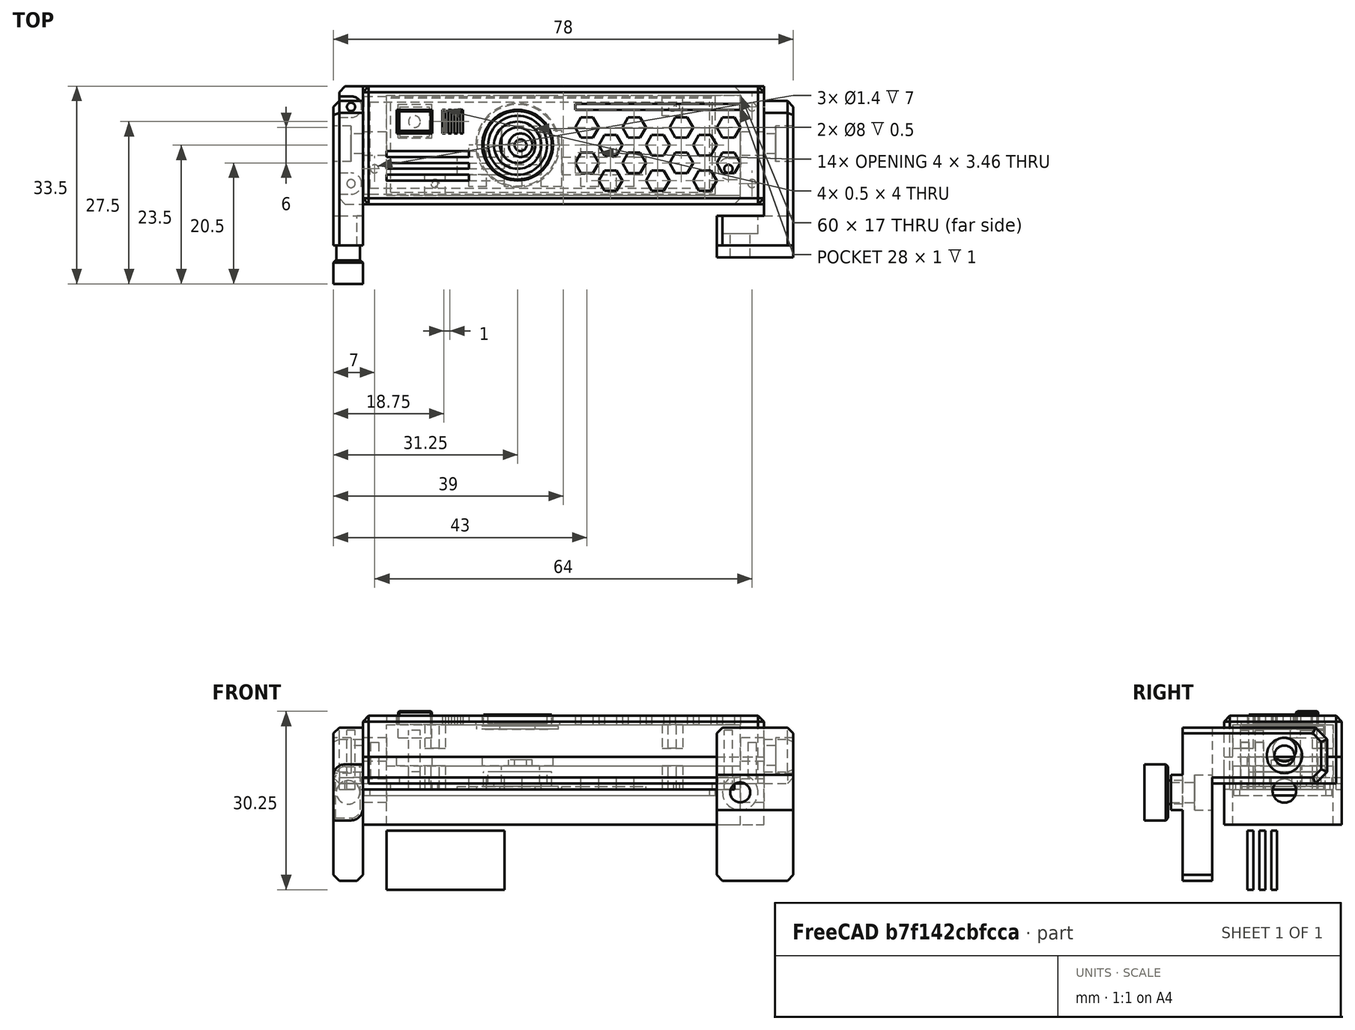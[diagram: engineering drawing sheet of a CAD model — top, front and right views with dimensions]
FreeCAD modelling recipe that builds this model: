
FCSTD DOCUMENT  (FreeCAD 0.18R16146 (Git))
Label: camera-body
License: All rights reserved
LicenseURL: http://en.wikipedia.org/wiki/All_rights_reserved
objects: Part::Box×40, Part::Cylinder×34, Part::Cut×31, Part::MultiFuse×22, Part::Feature×21, Part::Chamfer×11, Part::Fillet×1
note: 160 computed .brp shape members not serialized (recipe doc carries the construction recipe); baked Part::Feature solids carry a one-line shape summary decoded from their .brp

FEATURE [Part::Box] Box  label="Cube"
  AttacherType = Attacher::AttachEngine3D
  Height = 1
  Length = 54.5
  Width = 16
FEATURE [Part::Cylinder] Cylinder
  Angle = 360
  AttacherType = Attacher::AttachEngine3D
  Height = 10
  Placement = pos=(7.5,1.5,0) rot=(0,0,1;0rad)
  Radius = 0.7
FEATURE [Part::Cylinder] Cylinder001
  Angle = 360
  AttacherType = Attacher::AttachEngine3D
  Height = 10
  Placement = pos=(47.75,14.5,0) rot=(0,0,1;0rad)
  Radius = 0.7
FEATURE [Part::Cylinder] Cylinder002
  Angle = 360
  AttacherType = Attacher::AttachEngine3D
  Height = 10
  Placement = pos=(48.5,14.5,0) rot=(0,0,1;0rad)
  Radius = 0.5
FEATURE [Part::Cylinder] Cylinder003
  Angle = 360
  AttacherType = Attacher::AttachEngine3D
  Height = 10
  Placement = pos=(7.5,1.5,0) rot=(0,0,1;0rad)
  Radius = 0.5
FEATURE [Part::MultiFuse] Fusion
  Shapes = -> [Cylinder003,Cylinder002]
FEATURE [Part::Cut] Cut
  Base = -> Box
  Tool = -> Fusion
FEATURE [Part::Cylinder] Cylinder004
  Angle = 360
  AttacherType = Attacher::AttachEngine3D
  Height = 3
  Placement = pos=(4,12,0) rot=(0,0,1;0rad)
  Radius = 1
FEATURE [Part::Box] Box001  label="Cube001"
  AttacherType = Attacher::AttachEngine3D
  Height = 2
  Length = 5
  Placement = pos=(1.5,9.5,0) rot=(0,0,1;0rad)
  Width = 5
FEATURE [Part::Box] Box002  label="Cube002"
  AttacherType = Attacher::AttachEngine3D
  Height = 4
  Length = 6.5
  Placement = pos=(18.75,4.75,0) rot=(0,0,1;0rad)
  Width = 6.5
FEATURE [Part::Cylinder] Cylinder005
  Angle = 360
  AttacherType = Attacher::AttachEngine3D
  Height = 5
  Placement = pos=(22,8,0) rot=(0,0,1;0rad)
  Radius = 2
FEATURE [Part::Cylinder] Cylinder006
  Angle = 360
  AttacherType = Attacher::AttachEngine3D
  Height = 5
  Placement = pos=(22,8,0) rot=(0,0,1;0rad)
  Radius = 1
FEATURE [Part::Cut] Cut001
  Base = -> Cylinder005
  Tool = -> Cylinder006
FEATURE [Part::MultiFuse] Fusion001
  Shapes = -> [Cut001,Box002]
FEATURE [Part::MultiFuse] Fusion002  label="pcb-pred"
  Placement = pos=(-27.25,0,0) rot=(0,0,1;0rad)
  Shapes = -> [Fusion001,Box001,Cylinder004,Cut]
FEATURE [Part::Box] Box003  label="Cube003"
  AttacherType = Attacher::AttachEngine3D
  Height = 11.5
  Length = 68
  Placement = pos=(-32,-2,-6) rot=(0,0,1;0rad)
  Width = 20
FEATURE [Part::Box] Box004  label="Cube004"
  AttacherType = Attacher::AttachEngine3D
  Height = 10
  Length = 60
  Placement = pos=(-28,-0.5,-6) rot=(0,0,1;0rad)
  Width = 17
FEATURE [Part::Cylinder] Cylinder007
  Angle = 360
  AttacherType = Attacher::AttachEngine3D
  Height = 10
  Placement = pos=(-5.75,8,0) rot=(0,0,1;0rad)
  Radius = 3.2
FEATURE [Part::Cylinder] Cylinder008
  Angle = 360
  AttacherType = Attacher::AttachEngine3D
  Height = 10
  Placement = pos=(-23.25,12,0) rot=(0,0,1;0rad)
  Radius = 1
FEATURE [Part::Box] Box005  label="Cube005"
  AttacherType = Attacher::AttachEngine3D
  Height = 5
  Length = 3.5
  Placement = pos=(-21.5,-2,0) rot=(0,0,1;0rad)
  Width = 5
FEATURE [Part::Box] Box006  label="Cube006"
  AttacherType = Attacher::AttachEngine3D
  Height = 5
  Length = 3.5
  Placement = pos=(18.75,13,0) rot=(0,0,1;0rad)
  Width = 5
FEATURE [Part::MultiFuse] Fusion003003
  Placement = pos=(-27.25,0,-6) rot=(0,0,1;0rad)
  Shapes = -> [Cylinder,Cylinder001]
FEATURE [Part::Cut] Cut002
  Base = -> Box003
  Tool = -> Box004
FEATURE [Part::Cut] Cut003
  Base = -> Cut002
  Tool = -> Cylinder007
FEATURE [Part::MultiFuse] Fusion003004
  Shapes = -> [Box005,Box006]
FEATURE [Part::MultiFuse] Fusion003005
  Shapes = -> [Cut003,Fusion003004]
FEATURE [Part::Cut] Cut004
  Base = -> Fusion003005
  Tool = -> Fusion003003
FEATURE [Part::Box] Box007  label="Cube007"
  AttacherType = Attacher::AttachEngine3D
  Height = 10
  Length = 6
  Placement = pos=(-26.25,10,0) rot=(0,0,1;0rad)
  Width = 4
FEATURE [Part::Cut] Cut005
  Base = -> Cut004
  Tool = -> Box007
FEATURE [Part::Cylinder] Cylinder009
  Angle = 360
  AttacherType = Attacher::AttachEngine3D
  Height = 10
  Placement = pos=(-5.75,8,0) rot=(0,0,1;0rad)
  Radius = 6
FEATURE [Part::Cut] Cut006
  Base = -> Cut005
  Tool = -> Cylinder009
FEATURE [Part::Cylinder] Cylinder010
  Angle = 360
  AttacherType = Attacher::AttachEngine3D
  Height = 10
  Placement = pos=(-27,8.25,-0.25) rot=(0,-1,0;1.5708rad)
  Radius = 2
FEATURE [Part::Cylinder] Cylinder011
  Angle = 360
  AttacherType = Attacher::AttachEngine3D
  Height = 10
  Placement = pos=(37,8.25,-0.25) rot=(0,-1,0;1.5708rad)
  Radius = 2
FEATURE [Part::MultiFuse] Fusion003006
  Shapes = -> [Cylinder011,Cylinder010]
FEATURE [Part::Cut] Cut007
  Base = -> Cut006
  Tool = -> Fusion003006
FEATURE [Part::Feature] Cut007001  label="Cut008"
  shape: bbox 68 x 20 x 11.5 mm, 30 faces (baked)
FEATURE [Part::Chamfer] Chamfer
  Base = -> Cut007001
  Edges = 8 edges r=1: [Edge1,Edge2,Edge4,Edge6,Edge7,Edge8,Edge23,Edge24]
  Placement = pos=(1e-15,0,-7) rot=(0,1,0;3.14159rad)
FEATURE [Part::Cylinder] Cylinder012
  Angle = 360
  AttacherType = Attacher::AttachEngine3D
  Height = 10
  Placement = pos=(-34,14.5,0) rot=(0,0,1;0rad)
  Radius = 0.7
FEATURE [Part::Cylinder] Cylinder013
  Angle = 360
  AttacherType = Attacher::AttachEngine3D
  Height = 10
  Placement = pos=(-34,1.5,0) rot=(0,0,1;0rad)
  Radius = 0.7
FEATURE [Part::Cylinder] Cylinder014
  Angle = 360
  AttacherType = Attacher::AttachEngine3D
  Height = 10
  Placement = pos=(30,4,0) rot=(0,0,1;0rad)
  Radius = 0.7
FEATURE [Part::MultiFuse] Fusion003007
  Shapes = -> [Cylinder014,Cylinder013,Cylinder012]
FEATURE [Part::Feature] Fusion003007001  label="Fusion003008"
  Placement = pos=(0,0,-8) rot=(0,0,1;0rad)
  shape: bbox 65.4 x 14.4 x 10 mm, 9 faces, 3 solids (baked)
FEATURE [Part::Cut] Cut007002
  Base = -> Chamfer
  Tool = -> Fusion003007001
FEATURE [Part::Box] Box008  label="Cube008"
  AttacherType = Attacher::AttachEngine3D
  Height = 2
  Length = 68
  Placement = pos=(-36,-2,0) rot=(0,0,1;0rad)
  Width = 20
FEATURE [Part::Chamfer] Chamfer001
  Base = -> Box008
  Edges = 4 edges r=1: [Edge1,Edge3,Edge5,Edge7]
FEATURE [Part::Box] Box009  label="Cube009"
  AttacherType = Attacher::AttachEngine3D
  Height = 1
  Length = 59.6
  Placement = pos=(-31.8,-0.3,0) rot=(0,0,1;0rad)
  Width = 1
FEATURE [Part::Box] Box010  label="Cube010"
  AttacherType = Attacher::AttachEngine3D
  Height = 1
  Length = 59.6
  Placement = pos=(-31.8,15.3,0) rot=(0,0,1;0rad)
  Width = 1
FEATURE [Part::Box] Box011  label="Cube011"
  AttacherType = Attacher::AttachEngine3D
  Height = 1
  Length = 1
  Placement = pos=(-31.8,-0.3,0) rot=(0,0,1;0rad)
  Width = 16
FEATURE [Part::Box] Box012  label="Cube012"
  AttacherType = Attacher::AttachEngine3D
  Height = 1
  Length = 1
  Placement = pos=(26.8,-0.3,0) rot=(0,0,1;0rad)
  Width = 16
FEATURE [Part::MultiFuse] Fusion003007002
  Placement = pos=(0,0,-1) rot=(0,0,1;0rad)
  Shapes = -> [Box012,Box011,Box010,Box009]
FEATURE [Part::MultiFuse] Fusion003007003
  Shapes = -> [Fusion003007002,Chamfer001]
FEATURE [Part::Feature] Fusion003007004
  shape: bbox 65.4 x 14.4 x 10 mm, 9 faces, 3 solids (baked)
FEATURE [Part::Cut] Cut007003
  Base = -> Fusion003007003
  Tool = -> Fusion003007004
FEATURE [Part::Cylinder] Cylinder015
  Angle = 360
  AttacherType = Attacher::AttachEngine3D
  Height = 1
  Placement = pos=(-34,1.5,0) rot=(0,0,1;0rad)
  Radius = 1
FEATURE [Part::Cylinder] Cylinder016
  Angle = 360
  AttacherType = Attacher::AttachEngine3D
  Height = 1
  Placement = pos=(-34,14.5,0) rot=(0,0,1;0rad)
  Radius = 1
FEATURE [Part::Cylinder] Cylinder017
  Angle = 360
  AttacherType = Attacher::AttachEngine3D
  Height = 1
  Placement = pos=(30,4,0) rot=(0,0,1;0rad)
  Radius = 1
FEATURE [Part::MultiFuse] Fusion003007005
  Placement = pos=(0,0,1) rot=(0,0,1;0rad)
  Shapes = -> [Cylinder017,Cylinder016,Cylinder015]
FEATURE [Part::Cut] Cut007004
  Base = -> Cut007003
  Tool = -> Fusion003007005
FEATURE [Part::Box] Box013  label="Cube013"
  AttacherType = Attacher::AttachEngine3D
  Height = 10
  Length = 3
  Width = 2
FEATURE [Part::Box] Box014  label="Cube014"
  AttacherType = Attacher::AttachEngine3D
  Height = 10
  Length = 3
  Placement = pos=(0,5,0) rot=(0,0,1;0rad)
  Width = 2
FEATURE [Part::MultiFuse] Fusion003007006
  Placement = pos=(0,1,-3) rot=(0,0,1;0rad)
  Shapes = -> [Box014,Box013]
FEATURE [Part::Feature] Fusion003007006001  label="Fusion003007007"
  Placement = pos=(6,1,-3) rot=(0,0,1;0rad)
  shape: bbox 3 x 7 x 10 mm, 12 faces, 2 solids (baked)
FEATURE [Part::Feature] Fusion003007006002  label="Fusion003007008"
  Placement = pos=(-8,1,-3) rot=(0,0,1;0rad)
  shape: bbox 3 x 7 x 10 mm, 12 faces, 2 solids (baked)
FEATURE [Part::Feature] Fusion003007006003  label="Fusion003007009"
  Placement = pos=(-14,1,-3) rot=(0,0,1;0rad)
  shape: bbox 3 x 7 x 10 mm, 12 faces, 2 solids (baked)
FEATURE [Part::Box] Box015  label="Cube015"
  AttacherType = Attacher::AttachEngine3D
  Height = 10
  Length = 3.5
  Placement = pos=(-1.75,1,-6) rot=(0,0,1;0rad)
  Width = 9.5
FEATURE [Part::MultiFuse] Fusion003007006004
  Placement = pos=(5,0,0) rot=(0,0,1;0rad)
  Shapes = -> [Fusion003007006001,Fusion003007006]
FEATURE [Part::MultiFuse] Fusion003007006005
  Shapes = -> [Fusion003007006002,Fusion003007006003]
FEATURE [Part::Box] Box016  label="Cube016"
  AttacherType = Attacher::AttachEngine3D
  Height = 0.5
  Length = 32
  Placement = pos=(-16,3,0) rot=(0,0,1;0rad)
  Width = 3
FEATURE [Part::Cut] Cut007005
  Base = -> Cut007004
  Tool = -> Fusion003007006004
FEATURE [Part::Cut] Cut007006
  Base = -> Cut007005
  Tool = -> Box015
FEATURE [Part::Cut] Cut007007
  Base = -> Cut007006
  Tool = -> Fusion003007006005
FEATURE [Part::Cylinder] Cylinder018
  Angle = 360
  AttacherType = Attacher::AttachEngine3D
  Height = 10
  Placement = pos=(5.75,8,-11.5) rot=(0,0,1;0rad)
  Radius = 7.1
FEATURE [Part::Cut] Cut007009
  Base = -> Cut007002
  Tool = -> Cylinder018
FEATURE [Part::Box] Box017  label="Cube017"
  AttacherType = Attacher::AttachEngine3D
  Height = 10
  Length = 0.5
  Placement = pos=(18,10,-17) rot=(0,0,1;0rad)
  Width = 4
FEATURE [Part::Box] Box018  label="Cube018"
  AttacherType = Attacher::AttachEngine3D
  Height = 10
  Length = 0.5
  Placement = pos=(16,10,-17) rot=(0,0,1;0rad)
  Width = 4
FEATURE [Part::Box] Box019  label="Cube019"
  AttacherType = Attacher::AttachEngine3D
  Height = 10
  Length = 0.5
  Placement = pos=(17,10,-17) rot=(0,0,1;0rad)
  Width = 4
FEATURE [Part::Box] Box020  label="Cube020"
  AttacherType = Attacher::AttachEngine3D
  Height = 10
  Length = 0.5
  Placement = pos=(15,10,-17) rot=(0,0,1;0rad)
  Width = 4
FEATURE [Part::MultiFuse] Fusion003007006006
  Shapes = -> [Box020,Box019,Box018,Box017]
FEATURE [Part::Cut] Cut007010
  Base = -> Cut007009
  Tool = -> Fusion003007006006
FEATURE [Part::Box] Box021  label="Cube021"
  AttacherType = Attacher::AttachEngine3D
  Height = 10
  Length = 20
  Placement = pos=(-28,2,-17) rot=(0,0,1;0rad)
  Width = 1
FEATURE [Part::Box] Box022  label="Cube022"
  AttacherType = Attacher::AttachEngine3D
  Height = 10
  Length = 20
  Placement = pos=(-28,4,-17) rot=(0,0,1;0rad)
  Width = 1
FEATURE [Part::Box] Box023  label="Cube023"
  AttacherType = Attacher::AttachEngine3D
  Height = 10
  Length = 20
  Placement = pos=(-28,6,-17) rot=(0,0,1;0rad)
  Width = 1
FEATURE [Part::Feature] Body003
  Placement = pos=(-6,11,-19) rot=(0,0,1;0rad)
  shape: bbox 4 x 3.464 x 10 mm, 8 faces (baked)
FEATURE [Part::Feature] Body004
  Placement = pos=(-10,8,-19) rot=(0,0,1;0rad)
  shape: bbox 4 x 3.464 x 10 mm, 8 faces (baked)
FEATURE [Part::Feature] Body005
  Placement = pos=(-14,11,-19) rot=(0,0,1;0rad)
  shape: bbox 4 x 3.464 x 10 mm, 8 faces (baked)
FEATURE [Part::Feature] Body006
  Placement = pos=(-18,8,-19) rot=(0,0,1;0rad)
  shape: bbox 4 x 3.464 x 10 mm, 8 faces (baked)
FEATURE [Part::Feature] Body007
  Placement = pos=(-22,11,-19) rot=(0,0,1;0rad)
  shape: bbox 4 x 3.464 x 10 mm, 8 faces (baked)
FEATURE [Part::Feature] Body008
  Placement = pos=(-26,8,-19) rot=(0,0,1;0rad)
  shape: bbox 4 x 3.464 x 10 mm, 8 faces (baked)
FEATURE [Part::Feature] Body009
  Placement = pos=(-30,11,-19) rot=(0,0,1;0rad)
  shape: bbox 4 x 3.464 x 10 mm, 8 faces (baked)
FEATURE [Part::Feature] Body010
  Placement = pos=(-6,5,-19) rot=(0,0,1;0rad)
  shape: bbox 4 x 3.464 x 10 mm, 8 faces (baked)
FEATURE [Part::Feature] Body011
  Placement = pos=(-14,5,-19) rot=(0,0,1;0rad)
  shape: bbox 4 x 3.464 x 10 mm, 8 faces (baked)
FEATURE [Part::Feature] Body012
  Placement = pos=(-22,5,-19) rot=(0,0,1;0rad)
  shape: bbox 4 x 3.464 x 10 mm, 8 faces (baked)
FEATURE [Part::Feature] Body013
  Placement = pos=(-30,5,-19) rot=(0,0,1;0rad)
  shape: bbox 4 x 3.464 x 10 mm, 8 faces (baked)
FEATURE [Part::Feature] Body014
  Placement = pos=(-10,2,-19) rot=(0,0,1;0rad)
  shape: bbox 4 x 3.464 x 10 mm, 8 faces (baked)
FEATURE [Part::Feature] Body015
  Placement = pos=(-18,2,-19) rot=(0,0,1;0rad)
  shape: bbox 4 x 3.464 x 10 mm, 8 faces (baked)
FEATURE [Part::Feature] Body016
  Placement = pos=(-26,2,-19) rot=(0,0,1;0rad)
  shape: bbox 4 x 3.464 x 10 mm, 8 faces (baked)
FEATURE [Part::MultiFuse] Fusion003007006007
  Shapes = -> [Body003,Body004,Body005,Body006,Body008,Body007,Body009,Body010,Body011,Body012,Body013,Body016,Body015,Body014]
FEATURE [Part::Cut] Cut007011
  Base = -> Cut007010
  Tool = -> Fusion003007006007
FEATURE [Part::Box] Box024  label="Cube024"
  AttacherType = Attacher::AttachEngine3D
  Height = 10
  Length = 28
  Placement = pos=(-32,14,-21.5) rot=(0,0,1;0rad)
  Width = 1
FEATURE [Part::Box] Box025  label="Cube025"
  AttacherType = Attacher::AttachEngine3D
  Height = 10
  Length = 14
  Placement = pos=(14,7,-21) rot=(0,0,1;0rad)
  Width = 1
FEATURE [Part::Box] Box026  label="Cube026"
  AttacherType = Attacher::AttachEngine3D
  Height = 10
  Length = 14
  Placement = pos=(14,5,-21) rot=(0,0,1;0rad)
  Width = 1
FEATURE [Part::Box] Box027  label="Cube027"
  AttacherType = Attacher::AttachEngine3D
  Height = 10
  Length = 14
  Placement = pos=(14,3,-21) rot=(0,0,1;0rad)
  Width = 1
FEATURE [Part::MultiFuse] Fusion003007006008
  Placement = pos=(0,-1,-0.5) rot=(0,0,1;0rad)
  Shapes = -> [Box027,Box025,Box026]
FEATURE [Part::Cut] Cut007012
  Base = -> Cut007011
  Tool = -> Box024
FEATURE [Part::Cut] Cut007013
  Base = -> Cut007012
  Placement = pos=(0,0,0) rot=(0,1,0;3.14159rad)
  Tool = -> Fusion003007006008
FEATURE [Part::Box] Box028  label="Cube028"
  AttacherType = Attacher::AttachEngine3D
  Height = 4.5
  Length = 5.7
  Width = 3.7
FEATURE [Part::Box] Box029  label="Cube029"
  AttacherType = Attacher::AttachEngine3D
  Height = 2.3
  Length = 5.7
  Placement = pos=(0,-1,0) rot=(0,0,1;0rad)
  Width = 5.7
FEATURE [Part::Cylinder] Cylinder019
  Angle = 360
  AttacherType = Attacher::AttachEngine3D
  Height = 0.5
  Placement = pos=(-5.75,8,0) rot=(0,0,1;0rad)
  Radius = 6.9
FEATURE [Part::Cylinder] Cylinder020
  Angle = 360
  AttacherType = Attacher::AttachEngine3D
  Height = 3
  Placement = pos=(-5.75,8,0) rot=(0,0,1;0rad)
  Radius = 5.8
FEATURE [Part::Cylinder] Cylinder021
  Angle = 360
  AttacherType = Attacher::AttachEngine3D
  Height = 2.5
  Placement = pos=(-5.75,8,0.5) rot=(0,0,1;0rad)
  Radius = 4
FEATURE [Part::Cylinder] Cylinder022
  Angle = 360
  AttacherType = Attacher::AttachEngine3D
  Height = 4
  Placement = pos=(-5.75,8,0) rot=(0,0,1;0rad)
  Radius = 3
FEATURE [Part::Cylinder] Cylinder023
  Angle = 360
  AttacherType = Attacher::AttachEngine3D
  Height = 2.5
  Placement = pos=(-5.75,8,1) rot=(0,0,1;0rad)
  Radius = 5
FEATURE [Part::MultiFuse] Fusion003007006010
  Shapes = -> [Cylinder020,Cylinder019]
FEATURE [Part::Cut] Cut007014
  Base = -> Fusion003007006010
  Tool = -> Cylinder022
FEATURE [Part::Cut] Cut007015
  Base = -> Cut007014
  Tool = -> Cylinder021
FEATURE [Part::Cut] Cut007016  label="lens"
  Base = -> Cut007015
  Tool = -> Cylinder023
FEATURE [Part::Feature] Cut007016001  label="lens001"
  shape: bbox 13.8 x 13.8 x 3 mm, 11 faces (baked)
FEATURE [Part::Box] Box030  label="Cube030"
  AttacherType = Attacher::AttachEngine3D
  Height = 10
  Length = 21
  Placement = pos=(-14.5,0,2.5) rot=(0,0,1;0rad)
  Width = 18
FEATURE [Part::Cut] Cut007016002  label="lens-short"
  Base = -> Cut007016001
  Placement = pos=(0,0,10.2) rot=(0,0,1;0rad)
  Tool = -> Box030
FEATURE [Part::Box] Box032  label="Cube032"
  AttacherType = Attacher::AttachEngine3D
  Height = 9.5
  Length = 5
  Placement = pos=(-37,-9,1) rot=(0,0,1;0rad)
  Width = 24.5
FEATURE [Part::Box] Box033  label="Cube033"
  AttacherType = Attacher::AttachEngine3D
  Height = 9.5
  Length = 5
  Placement = pos=(36,-9,1) rot=(0,0,1;0rad)
  Width = 24.5
FEATURE [Part::Box] Box034  label="Cube034"
  AttacherType = Attacher::AttachEngine3D
  Height = 9.5
  Length = 5
  Placement = pos=(-37,-15,1) rot=(0,0,1;0rad)
  Width = 4
FEATURE [Part::Fillet] Fillet
  Base = -> Box034
  Edges = 2 edges r=2: [Edge2,Edge8]
  Placement = pos=(0,-0.25,-6.25) rot=(0,0,1;0rad)
FEATURE [Part::Chamfer] Chamfer005
  Base = -> Box032
  Edges = 2 edges r=2: [Edge11,Edge12]
FEATURE [Part::Chamfer] Chamfer006
  Base = -> Chamfer005
  Edges = 5 edges r=1: [Edge1,Edge2,Edge4,Edge5,Edge6]
FEATURE [Part::Chamfer] Chamfer007
  Base = -> Box033
  Edges = 2 edges r=2: [Edge11,Edge12]
FEATURE [Part::Chamfer] Chamfer008
  Base = -> Chamfer007
  Edges = 5 edges r=1: [Edge9,Edge11,Edge14,Edge17,Edge18]
FEATURE [Part::Box] Box036  label="Cube036"
  AttacherType = Attacher::AttachEngine3D
  Height = 6
  Length = 13
  Placement = pos=(28,-11,-3.5) rot=(0,0,1;0rad)
  Width = 2
FEATURE [Part::Box] Box037  label="Cube037"
  AttacherType = Attacher::AttachEngine3D
  Height = 26
  Length = 13
  Placement = pos=(28,-9,-15.5) rot=(0,0,1;0rad)
  Width = 5
FEATURE [Part::Chamfer] Chamfer009
  Base = -> Box037
  Edges = 1 edges r=1: [Edge6]
FEATURE [Part::Chamfer] Chamfer010
  Base = -> Chamfer009
  Edges = 3 edges r=1: [Edge3,Edge11,Edge15]
FEATURE [Part::MultiFuse] Fusion003007006011
  Shapes = -> [Chamfer010,Box036,Chamfer008]
FEATURE [Part::Box] Box038  label="Cube038"
  AttacherType = Attacher::AttachEngine3D
  Height = 26
  Length = 5
  Placement = pos=(-37,-9,-15.5) rot=(0,0,1;0rad)
  Width = 5
FEATURE [Part::Chamfer] Chamfer011
  Base = -> Box038
  Edges = 3 edges r=1: [Edge2,Edge4,Edge8]
FEATURE [Part::Cylinder] Cylinder024
  Angle = 360
  AttacherType = Attacher::AttachEngine3D
  Height = 3
  Placement = pos=(-34,8.25,5.75) rot=(0,-1,0;1.5708rad)
  Radius = 3
FEATURE [Part::Cylinder] Cylinder025
  Angle = 360
  AttacherType = Attacher::AttachEngine3D
  Height = 3
  Placement = pos=(41,8.25,5.75) rot=(0,-1,0;1.5708rad)
  Radius = 3
FEATURE [Part::Cylinder] Cylinder026
  Angle = 360
  AttacherType = Attacher::AttachEngine3D
  Height = 10
  Placement = pos=(41,8.25,5.75) rot=(0,-1,0;1.5708rad)
  Radius = 1.7
FEATURE [Part::Cylinder] Cylinder027
  Angle = 360
  AttacherType = Attacher::AttachEngine3D
  Height = 10
  Placement = pos=(-27,8.25,5.75) rot=(0,-1,0;1.5708rad)
  Radius = 1.7
FEATURE [Part::Cut] Cut007016003
  Base = -> Fusion003007006011
  Tool = -> Cylinder026
FEATURE [Part::Cut] Cut007016006
  Base = -> Cut007016003
  Tool = -> Cylinder025
FEATURE [Part::Cylinder] Cylinder028
  Angle = 360
  AttacherType = Attacher::AttachEngine3D
  Height = 10
  Placement = pos=(32,-14,-0.5) rot=(-1,0,0;1.5708rad)
  Radius = 1.7
FEATURE [Part::Cylinder] Cylinder029
  Angle = 360
  AttacherType = Attacher::AttachEngine3D
  Height = 3
  Placement = pos=(32,-7,-0.5) rot=(-1,0,0;1.5708rad)
  Radius = 3
FEATURE [Part::Cut] Cut007016007
  Base = -> Cut007016006
  Tool = -> Cylinder028
FEATURE [Part::Cut] Cut007016008
  Base = -> Cut007016007
  Tool = -> Cylinder029
FEATURE [Part::Chamfer] Chamfer012
  Base = -> Box028
  Edges = 7 edges r=0.2: [Edge1,Edge2,Edge5,Edge6,Edge7,Edge10,Edge12]
FEATURE [Part::MultiFuse] Fusion003007006013  label="btn"
  Placement = pos=(-26,10.25,8.75) rot=(0,0,1;0rad)
  Shapes = -> [Chamfer012,Box029]
FEATURE [Part::Cylinder] Cylinder030
  Angle = 360
  AttacherType = Attacher::AttachEngine3D
  Height = 6
  Placement = pos=(-34.5,-7.5,-0.5) rot=(1,0,0;1.5708rad)
  Radius = 2
FEATURE [Part::Chamfer] Chamfer013
  Base = -> Fillet
  Edges = 6 edges r=0.4: [Edge4,Edge11,Edge12,Edge14,Edge15,Edge16]
  Placement = pos=(0,-0.25,0) rot=(0,0,1;0rad)
FEATURE [Part::MultiFuse] Fusion003007006014
  Shapes = -> [Chamfer013,Cylinder030,Chamfer011,Chamfer006]
FEATURE [Part::Cut] Cut007016009
  Base = -> Fusion003007006014
  Tool = -> Cylinder027
FEATURE [Part::Cut] Cut007016010
  Base = -> Cut007016009
  Tool = -> Cylinder024
FEATURE [Part::Cut] Cut007016011
  Base = -> Cut007007
  Tool = -> Box016
FEATURE [Part::Cylinder] Cylinder031
  Angle = 360
  AttacherType = Attacher::AttachEngine3D
  Height = 1
  Placement = pos=(-34,1.5,1) rot=(0,0,1;0rad)
  Radius = 1.8
FEATURE [Part::Cylinder] Cylinder032
  Angle = 360
  AttacherType = Attacher::AttachEngine3D
  Height = 1
  Placement = pos=(-34,14.5,1) rot=(0,0,1;0rad)
  Radius = 1.8
FEATURE [Part::Cylinder] Cylinder033
  Angle = 360
  AttacherType = Attacher::AttachEngine3D
  Height = 1
  Placement = pos=(30,4,1) rot=(0,0,1;0rad)
  Radius = 1.8
FEATURE [Part::Box] Box039  label="Cube039"
  AttacherType = Attacher::AttachEngine3D
  Height = 1
  Length = 3.6
  Placement = pos=(-37.6,-0.3,1) rot=(0,0,1;0rad)
  Width = 3.6
FEATURE [Part::Box] Box040  label="Cube040"
  AttacherType = Attacher::AttachEngine3D
  Height = 1
  Length = 3.6
  Placement = pos=(30,2.2,1) rot=(0,0,1;0rad)
  Width = 3.6
FEATURE [Part::Box] Box041  label="Cube041"
  AttacherType = Attacher::AttachEngine3D
  Height = 1
  Length = 3.6
  Placement = pos=(-37.6,12.7,1) rot=(0,0,1;0rad)
  Width = 3.6
FEATURE [Part::MultiFuse] Fusion003007006015
  Shapes = -> [Box041,Box040,Box039,Cylinder033,Cylinder032,Cylinder031]
FEATURE [Part::Cut] Cut007016012
  Base = -> Cut007016011
  Tool = -> Fusion003007006015
